# Revit family: HighSpeed_Door_ZIP1000_DE
name_source: partatom
category: Türen
units: mm (PartAtom-declared; Revit-internal decimal feet)

## family parameters
Basisbauteil = Wand
Beim Laden mit Abzugskörper schneiden = Nein
Gemeinsam genutzt = Nein
Immer vertikal = Ja
OmniClass-Nummer = 23.30.10.00
OmniClass-Titel = Doors
Raumberechnungspunkt = Nein

## types (1)
- HighSpeed_Door_ZIP1000_DE
    Antrieb Position Typ = rechts
    Antrieb Position Typ Id = 1
    Antrieb Typ = Mit Aufsteckantrieb
    Antriebs- / Wellenverkleidung Ausführung Typ = Verzinkt
    Antriebs- / Wellenverkleidung Material = Seuster - RAL 9002
    Antriebs- / Wellenverkleidung Typ = ohne
    Antriebs- / Wellenverkleidung Typ Id = 0
    Behang = PVC
    Behang Material = Seuster - RAL 5010
    Behang Sichtfeld = transparentes PVC
    Behang Sichtfeld Stärke = 2 mm  [stored 0.00656168 ft]
    Behang Sichtfeld Typ = ohne Sichtfeld
    Behang Sichtfeld Typ Id = 1
    Behang Stärke = 1 mm  [stored 0.00328084 ft]
    Breite = 3000 mm  [stored 9.84252 ft]
    CE-Kennzeichnung vorhanden = Ja
    Cal_Max Height = 5000 mm  [stored 16.4042 ft]
    Cal_Max Width = 5000 mm  [stored 16.4042 ft]
    Cal_Min Height = 2000 mm  [stored 6.56168 ft]
    Cal_Min Space Height = 500 mm  [stored 1.64042 ft]
    Cal_Min Width = 2000 mm  [stored 6.56168 ft]
    Cal_Motor Cover = Nein
    Cal_Vision Panel = Nein
    Cal_Vision Panel Cut = 5 mm  [stored 0.0164042 ft]
    DIN 276 Kostengruppe = 344
    Dicke = 0 mm  [stored 0 ft]
    Durchlässigkeit für sichtbares Licht = 0.0
    Einbauort = innere Wände
    Einbauort Id = 1
    Einbruchschutz = ohne
    Einsatzbereich (Temperatur) = 5° bis -40°C
    Feuerwiderstandsklasse = ohne
    Funktion = Innen
    Fußbodenaufbau = 0 mm  [stored 0 ft]
    Hersteller = Seuster
    Höhe = 3000 mm  [stored 9.84252 ft]
    Modell = ZIP 1000
    Montageart Typ = Wandanbindung seitlich
    Montageart Typ Id = 1
    Notöffnung = Service- und
    Platzbedarf Antriebsseite = 340 mm  [stored 1.11549 ft]
    Platzbedarf Lagerseite = 170 mm  [stored 0.557743 ft]
    Rohbaubreite = 3000 mm  [stored 9.84252 ft]
    Rohbauhöhe = 3000 mm  [stored 9.84252 ft]
    STLB Gewerk = 31
    STLB Leistungsbereich = Türen / Tore - Metall
    Schallschutz = ohne
    Schließkantensicherung = Lichtgitter
    Sichtfeld Höhe = 900 mm  [stored 2.95276 ft]
    Steuerung Typ = BK FU Z
    Steuerung Typ Id = 1
    Torlaufgeschwindigkeit Schließen = ca. 1,0 m / Sek.
    Torlaufgeschwindigkeit Öffnen = ca. 2,0 m / Sek.
    UK Sichtfeld Höhe = 1300 mm  [stored 4.26509 ft]
    URL = https://seuster.de
    URL 2 = https://www.ap-seuster.de
    URL 3 = https://www.seuster.de
    Umweltproduktdeklaration = EPD-HSEL-0.9.1
    Wandabschluss = Nach Basisbauteil
    Windlastklasse nach EN 12424 = Klasse 3
    Zarge Material = Seuster - RAL 9002

note: [stored X ft] marks values corroborated as IEEE doubles in the binary element streams (Revit-internal decimal feet)

## geometry (parser evidence)
native form markers: Sweep x9
no freeform markers — native parametric forms only
